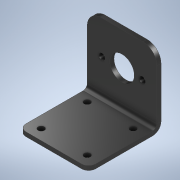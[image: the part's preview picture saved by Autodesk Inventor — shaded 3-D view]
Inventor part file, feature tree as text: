
AUTODESK INVENTOR PART (.ipt)
format: ipt  version: 2020 (Build 240168000, 168)  size: 170,496 bytes
history: native  units: mm
features: sheet_metal_op x4, sketch x3, other x3, fillet x2
ambient origin geometry x8: Origin, YZ Plane, XZ Plane, XY Plane, X Axis, Y Axis, Z Axis, Center Point
bodies: Solid1 (feature_tree)
feature tree (12):
  sheet_metal_op  "Face1"
  sheet_metal_op  "Flange1"
  fillet  "Fillet1"  Radius=50.0mm
  fillet  "Fillet2"  Radius=52.0mm
  sketch  "Sketch1"  dims[d2=17.6mm]
  other  "Plate1"
  sketch  "Sketch2"  dims[d3=24.0mm]
  other  "Plate2"
  sheet_metal_op  "Bend1"
  sheet_metal_op  "Corner1"
  sketch  "Sketch3"  dims[d4=4.5mm d5=4.5mm d6=29.0mm d7=14.5mm d8=24.0mm d9=24.0mm d10=25.0mm d11=3.0mm d12=3.0mm d13=1.5mm d14=6.0mm d15=3.0mm d16=52.0mm d17=90.0deg d18=3.0mm d19=12.0mm d20=3.0mm d21=3.0mm d22=10.0mm d23=5.0mm d24=33.0mm d25=33.0mm d26=24.0mm d27=25.0mm d28=4.5mm d29=4.5mm d30=4.5mm d31=4.5mm d32=3.0mm d33=0.0mm]
  other  "Cut1"
